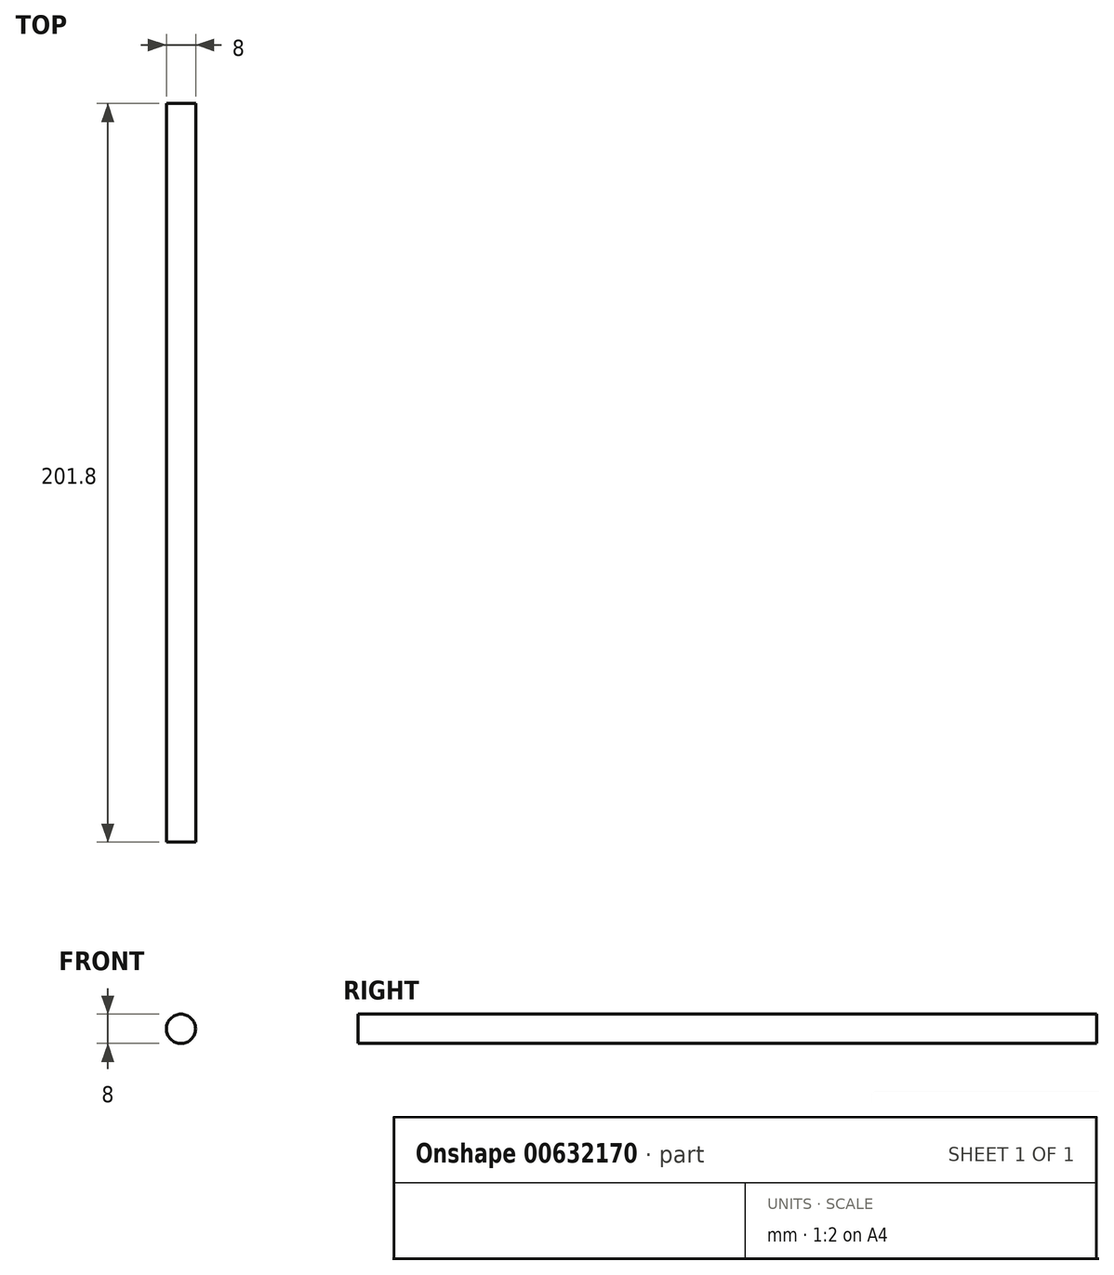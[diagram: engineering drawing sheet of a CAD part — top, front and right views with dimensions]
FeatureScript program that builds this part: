
annotation { "Feature Type Name" : "Feature", "Feature Type Description" : "" }
export const myFeature = defineFeature(function(context is Context, id is Id, definition is map)
    precondition{}
    {
        {
            var Q0;
            Q0=qCreatedBy(makeId("Front.planeOp"),FACE);
            var sketch = newSketch(context, id + "F0", { "sketchPlane" : qUnion([Q0])});
            skCircle(sketch, "E0", {"center": v(0, 0) * mm, "radius": 4 * mm});
            skSolve(sketch);
        }
        {
            var Q0;
            Q0 = qSketchRegion(id + "F0", true);
            extrude(context, id + "F1", {"entities" : qUnion([Q0]), "depth" : 201.8 * mm, "offsetDistance" : 25 * mm});
        }
    });
